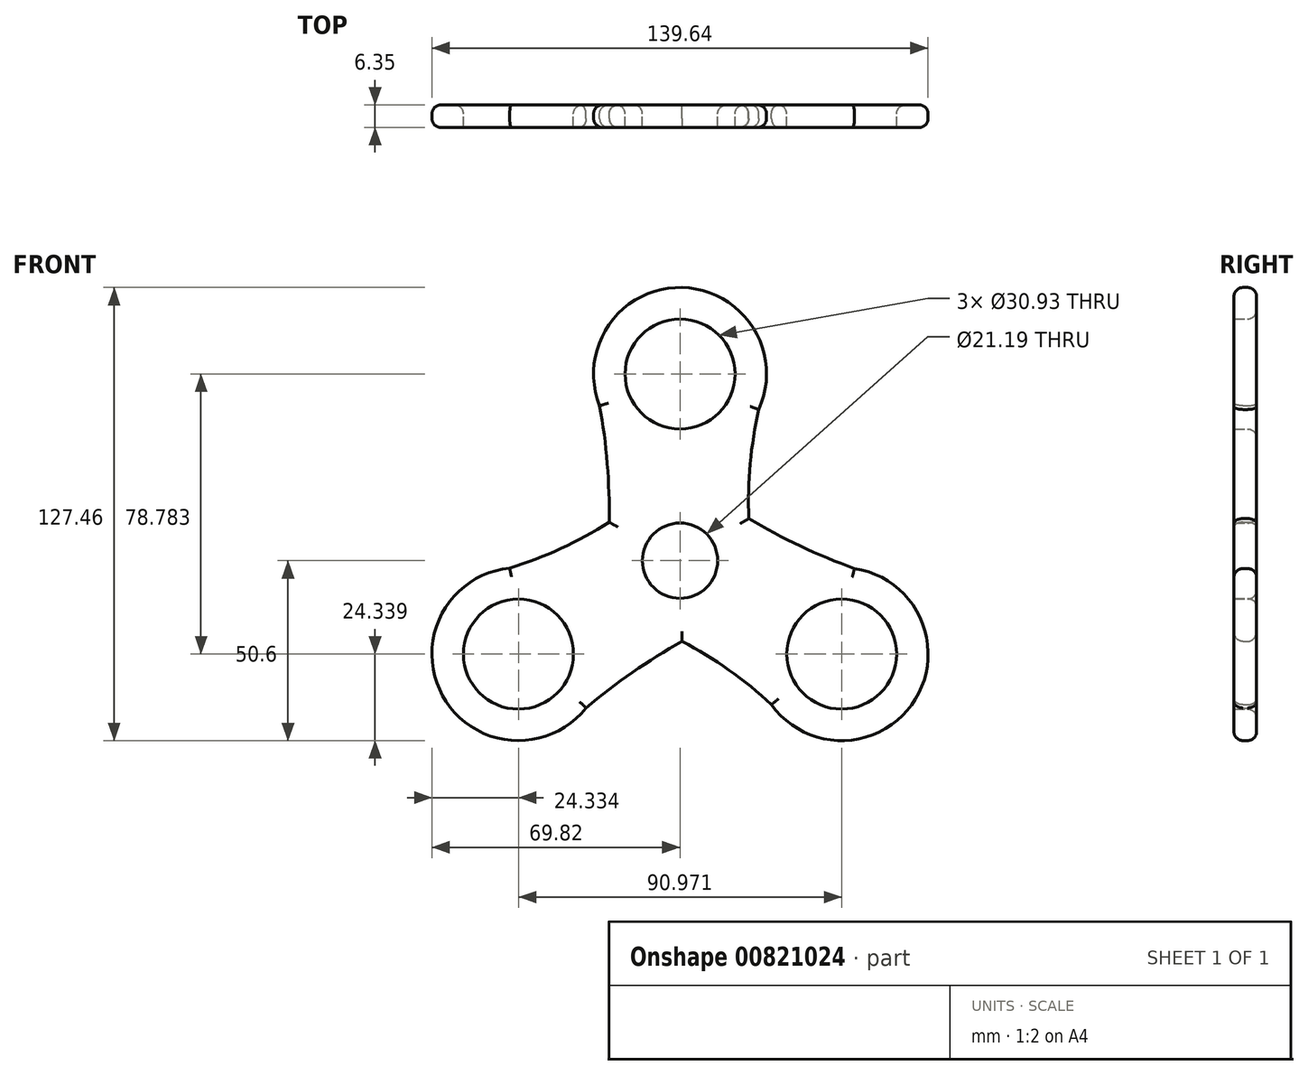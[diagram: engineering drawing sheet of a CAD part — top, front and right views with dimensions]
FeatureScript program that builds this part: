
annotation { "Feature Type Name" : "Feature", "Feature Type Description" : "" }
export const myFeature = defineFeature(function(context is Context, id is Id, definition is map)
    precondition{}
    {
        {
            var Q0;
            Q0=qCreatedBy(makeId("Front.planeOp"),FACE);
            var sketch = newSketch(context, id + "F0", { "sketchPlane" : qUnion([Q0])});
            skCircle(sketch, "E0", {"center": v(0, 0) * mm, "radius": 10.6 * mm});
            skCircle(sketch, "E1", {"center": v(0, 52.52) * mm, "radius": 15.47 * mm});
            skArc(sketch, "E2", {"start": v(22.2, 42.54) * mm, "mid": v(0.58, 76.85) * mm, "end": v(-22.65, 43.61) * mm});
            skArc(sketch, "E3", {"start": v(-19.96, 10.85) * mm, "mid": v(-20.87, 31.36) * mm, "end": v(-24.32, 51.6) * mm});
            skArc(sketch, "E4", {"start": v(24.21, 50.11) * mm, "mid": v(20.17, 31.2) * mm, "end": v(19.37, 11.86) * mm});
            skCircle(sketch, "E5.1.0", {"center": v(-45.49, -26.26) * mm, "radius": 15.47 * mm});
            skArc(sketch, "E5.1.1", {"start": v(-47.94, -2.05) * mm, "mid": v(-66.84, -37.92) * mm, "end": v(-26.45, -41.42) * mm});
            skArc(sketch, "E5.1.3", {"start": v(-55.5, -4.09) * mm, "mid": v(-37.1, 1.87) * mm, "end": v(-19.96, 10.85) * mm});
            skCircle(sketch, "E5.2.0", {"center": v(45.49, -26.26) * mm, "radius": 15.47 * mm});
            skArc(sketch, "E5.2.1", {"start": v(25.75, -40.5) * mm, "mid": v(66.26, -38.93) * mm, "end": v(49.1, -2.2) * mm});
            skArc(sketch, "E5.2.3", {"start": v(31.3, -46.03) * mm, "mid": v(16.93, -33.07) * mm, "end": v(0.58, -22.7) * mm});
            skArc(sketch, "E6.trimOffspring", {"start": v(19.37, 11.86) * mm, "mid": v(37.59, 2.4) * mm, "end": v(56.84, -4.74) * mm});
            skPoint(sketch, "E7.orphan", {"position": v(20.5, 0) * mm});
            skPoint(sketch, "E8.orphan", {"position": v(-20.5, 0) * mm});
            skArc(sketch, "E9.trimOffspring", {"start": v(0.58, -22.7) * mm, "mid": v(-16.72, -33.75) * mm, "end": v(-32.52, -46.85) * mm});
            skSolve(sketch);
        }
        {
            var Q0;
            Q0 = qSketchRegion(id + "F0", true);
            extrude(context, id + "F1", {"entities" : qUnion([Q0]), "depth" : 6.35 * mm, "offsetDistance" : 25.4 * mm});
        }
        {
            var Q0;
            Q0=makeQuery(id+"F1.opExtrude","CAP_EDGE",EDGE,{"disambiguationData":[OSD([sQuery(id+"F0.wireOp",EDGE,"E3")])],"isStart":false});
            var Q1;
            Q1=makeQuery(id+"F1.opExtrude","CAP_EDGE",EDGE,{"disambiguationData":[OSD([sQuery(id+"F0.wireOp",EDGE,"E2")])],"isStart":false});
            var Q2;
            Q2=makeQuery(id+"F1.opExtrude","CAP_EDGE",EDGE,{"disambiguationData":[OSD([sQuery(id+"F0.wireOp",EDGE,"E4")])],"isStart":false});
            var Q3;
            Q3=makeQuery(id+"F1.opExtrude","CAP_EDGE",EDGE,{"disambiguationData":[OSD([sQuery(id+"F0.wireOp",EDGE,"E6.trimOffspring")])],"isStart":false});
            var Q4;
            Q4=makeQuery(id+"F1.opExtrude","CAP_EDGE",EDGE,{"disambiguationData":[OSD([sQuery(id+"F0.wireOp",EDGE,"E5.2.1")])],"isStart":false});
            var Q5;
            Q5=makeQuery(id+"F1.opExtrude","CAP_EDGE",EDGE,{"disambiguationData":[OSD([sQuery(id+"F0.wireOp",EDGE,"E5.2.3")])],"isStart":false});
            var Q6;
            Q6=makeQuery(id+"F1.opExtrude","CAP_EDGE",EDGE,{"disambiguationData":[OSD([sQuery(id+"F0.wireOp",EDGE,"E9.trimOffspring")])],"isStart":false});
            var Q7;
            Q7=makeQuery(id+"F1.opExtrude","CAP_EDGE",EDGE,{"disambiguationData":[OSD([sQuery(id+"F0.wireOp",EDGE,"E5.1.1")])],"isStart":false});
            var Q8;
            Q8=makeQuery(id+"F1.opExtrude","CAP_EDGE",EDGE,{"disambiguationData":[OSD([sQuery(id+"F0.wireOp",EDGE,"E5.1.3")])],"isStart":false});
            fillet(context, id + "F2", {"entities" : qUnion([Q0, Q1, Q2, Q3, Q4, Q5, Q6, Q7, Q8]), "radius" : 2.54 * mm, "tangentPropagation" : true, "allowEdgeOverflow" : false});
        }
        {
            var Q0;
            Q0=makeQuery(id+"F1.opExtrude","CAP_EDGE",EDGE,{"disambiguationData":[OSD([sQuery(id+"F0.wireOp",EDGE,"E2")])],"isStart":true});
            var Q1;
            Q1=makeQuery(id+"F1.opExtrude","CAP_EDGE",EDGE,{"disambiguationData":[OSD([sQuery(id+"F0.wireOp",EDGE,"E3")])],"isStart":true});
            var Q2;
            Q2=makeQuery(id+"F1.opExtrude","CAP_EDGE",EDGE,{"disambiguationData":[OSD([sQuery(id+"F0.wireOp",EDGE,"E5.1.3")])],"isStart":true});
            var Q3;
            Q3=makeQuery(id+"F1.opExtrude","CAP_EDGE",EDGE,{"disambiguationData":[OSD([sQuery(id+"F0.wireOp",EDGE,"E5.1.1")])],"isStart":true});
            var Q4;
            Q4=makeQuery(id+"F1.opExtrude","CAP_EDGE",EDGE,{"disambiguationData":[OSD([sQuery(id+"F0.wireOp",EDGE,"E9.trimOffspring")])],"isStart":true});
            var Q5;
            Q5=makeQuery(id+"F1.opExtrude","CAP_EDGE",EDGE,{"disambiguationData":[OSD([sQuery(id+"F0.wireOp",EDGE,"E5.2.3")])],"isStart":true});
            var Q6;
            Q6=makeQuery(id+"F1.opExtrude","CAP_EDGE",EDGE,{"disambiguationData":[OSD([sQuery(id+"F0.wireOp",EDGE,"E5.2.1")])],"isStart":true});
            var Q7;
            Q7=makeQuery(id+"F1.opExtrude","CAP_EDGE",EDGE,{"disambiguationData":[OSD([sQuery(id+"F0.wireOp",EDGE,"E6.trimOffspring")])],"isStart":true});
            var Q8;
            Q8=makeQuery(id+"F1.opExtrude","CAP_FACE",FACE,{"disambiguationData":[OSD([sQuery(id+"F0.wireOp",EDGE,"E0"),sQuery(id+"F0.wireOp",EDGE,"E1"),sQuery(id+"F0.wireOp",EDGE,"E2"),sQuery(id+"F0.wireOp",EDGE,"E3"),sQuery(id+"F0.wireOp",EDGE,"E4"),sQuery(id+"F0.wireOp",EDGE,"E5.1.0"),sQuery(id+"F0.wireOp",EDGE,"E5.1.1"),sQuery(id+"F0.wireOp",EDGE,"E5.1.3"),sQuery(id+"F0.wireOp",EDGE,"E5.2.0"),sQuery(id+"F0.wireOp",EDGE,"E5.2.1"),sQuery(id+"F0.wireOp",EDGE,"E5.2.3"),sQuery(id+"F0.wireOp",EDGE,"E6.trimOffspring"),sQuery(id+"F0.wireOp",EDGE,"E9.trimOffspring")])],"isStart":true});
            fillet(context, id + "F3", {"entities" : qUnion([Q0, Q1, Q2, Q3, Q4, Q5, Q6, Q7, Q8]), "radius" : 2.54 * mm, "tangentPropagation" : true, "allowEdgeOverflow" : false});
        }
    });
